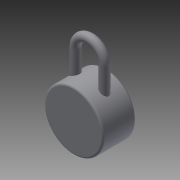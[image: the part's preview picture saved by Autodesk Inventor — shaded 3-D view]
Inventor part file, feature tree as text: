
AUTODESK INVENTOR PART (.ipt)
format: ipt  version: 2015 SP2 (Build 190223200, 223)  size: 1,182,720 bytes
history: native  units: mm
features: sketch x9, extrude x6, fillet x4, other x3, plane x2, revolve x1
ambient origin geometry x8: Origin, YZ Plane, XZ Plane, XY Plane, X Axis, Y Axis, Z Axis, Center Point
bodies: Solid1 (feature_tree)
feature tree (25):
  extrude  "Extrusion1"  Depth=29.57mm TaperAngle=0.0deg
  sketch  "Sketch2"  dims[d3=34.7mm d4=8.0mm]
  plane  "Work Plane1"
  extrude  "Extrusion2"  Depth=8.0mm
  sketch  "Sketch4"  dims[d9=8.0mm d10=90.0deg]
  other  "Work Point1"
  other  "Work Point2"
  other  "Work Axis1"
  revolve  "Revolution1"  [1 undecoded]
  sketch  "Sketch8"  dims[d19=1.5mm d20=1.0mm]
  extrude  "Extrusion3"  TaperAngle=90.0deg  [1 undecoded]
  extrude  "Extrusion4"  Depth=53.5mm
  fillet  "Fillet1"  Radius=0.5mm
  fillet  "Fillet2"  Radius=0.5mm
  fillet  "Fillet3"  Radius=2.0mm
  fillet  "Fillet4"  Radius=1.5mm
  plane  "Work Plane2"
  extrude  "Extrusion5"  Depth=1.0mm
  extrude  "Extrusion6"  Depth=13.0mm
  sketch  "Sketch1"  dims[d0=54.75mm d1=29.57mm d2=0.0mm]
  sketch  "Sketch3"  dims[d5=10.0mm d6=0.0mm d7=18.0mm d8=0.0mm]
  sketch  "Sketch5"  dims[d11=53.5mm d12=53.5mm d13=0.5mm d14=0.0mm d15=0.5mm d16=0.0mm d17=2.0mm d18=1.5mm]
  sketch  "Sketch9"  dims[d21=15.0mm d22=13.0mm]
  sketch  "Sketch10"  dims[d23=0.5mm d24=0.0mm]
  sketch  "Sketch11"  dims[d25=1.0mm d26=0.0mm]
note: 2 required parameter values undecoded (feature->parameter linkage not recoverable at this tier; creation-order binding heuristic only, values carry confidence <= 0.55)